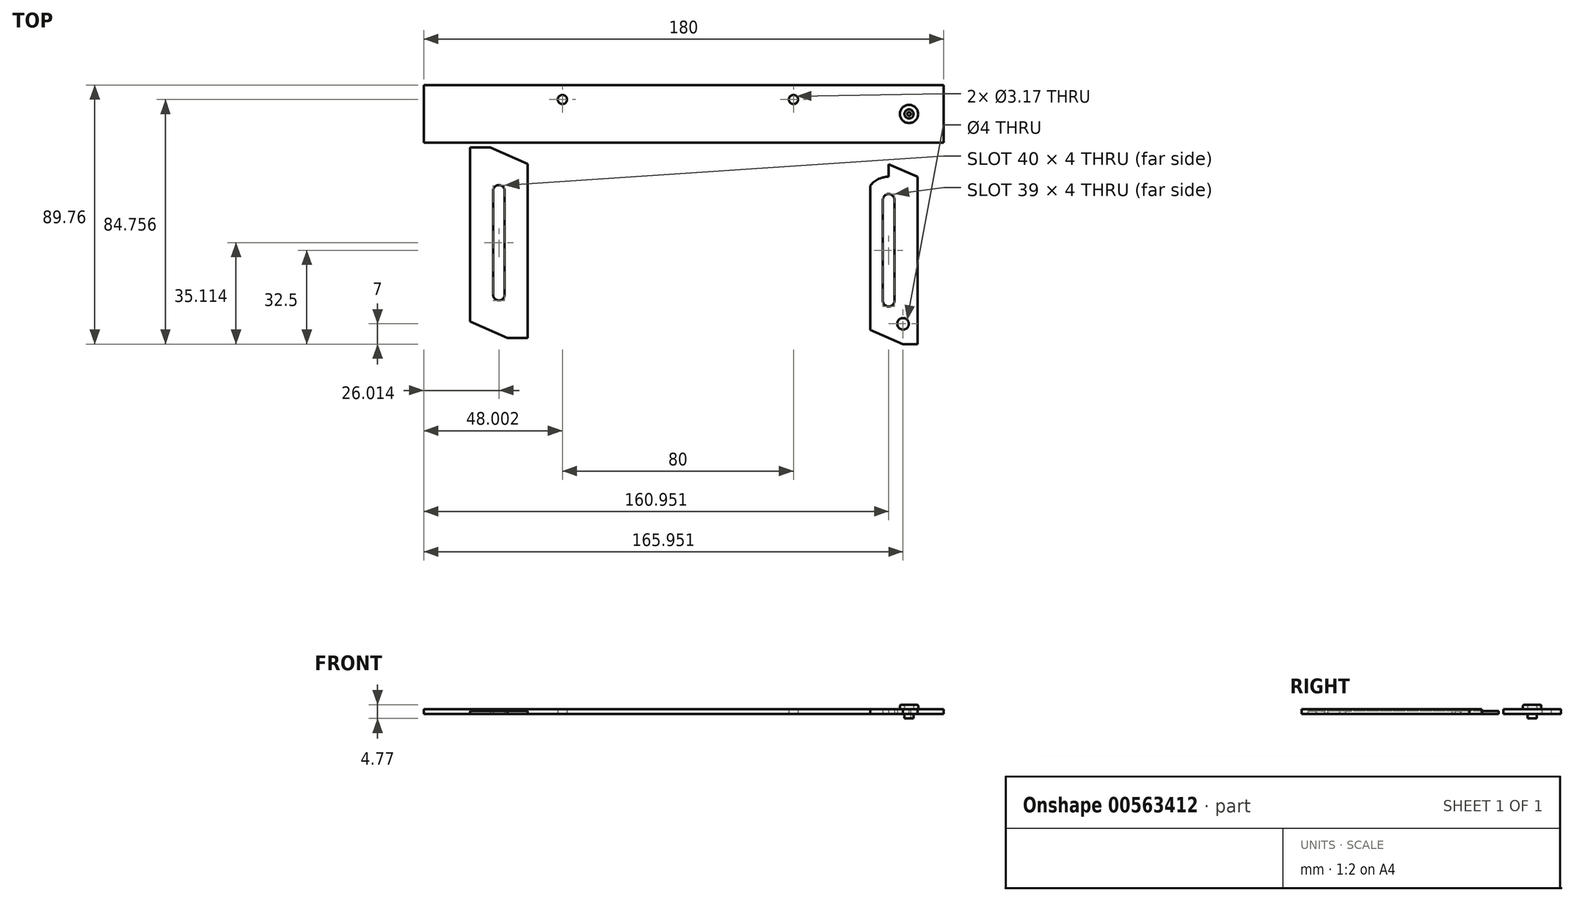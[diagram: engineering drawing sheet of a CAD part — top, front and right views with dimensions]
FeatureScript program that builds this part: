
annotation { "Feature Type Name" : "Feature", "Feature Type Description" : "" }
export const myFeature = defineFeature(function(context is Context, id is Id, definition is map)
    precondition{}
    {
        {
            var Q0;
            Q0=qCreatedBy(makeId("Top.planeOp"),FACE);
            var sketch = newSketch(context, id + "F0", { "sketchPlane" : qUnion([Q0])});
            skLineSegment(sketch, "E0.bottom", {"start": v(-55.85, 39.76) * mm, "end": v(124.15, 39.76) * mm});
            skLineSegment(sketch, "E0.top", {"start": v(-55.85, 19.76) * mm, "end": v(124.15, 19.76) * mm});
            skLineSegment(sketch, "E0.left", {"start": v(-55.85, 39.76) * mm, "end": v(-55.85, 19.76) * mm});
            skLineSegment(sketch, "E0.right", {"start": v(124.15, 39.76) * mm, "end": v(124.15, 19.76) * mm});
            skCircle(sketch, "E1", {"center": v(-7.85, 34.76) * mm, "radius": 1.59 * mm});
            skCircle(sketch, "E2", {"center": v(72.15, 34.76) * mm, "radius": 1.59 * mm});
            skCircle(sketch, "E3", {"center": v(112.15, 29.76) * mm, "radius": 1.59 * mm});
            skLineSegment(sketch, "E4", {"start": v(72.15, 34.76) * mm, "end": v(-7.85, 34.76) * mm, "construction": true});
            skSolve(sketch);
        }
        {
            var Q0;
            {var subQ1=sQuery(id+"F0.wireOp",EDGE,"E0.top");Q0=makeQuery(id+"F0.imprint","IMPRINT",FACE,{"disambiguationData":[TD([[makeQuery(id+"F0.imprint","IMPRINT",EDGE,{"derivedFrom":subQ1}),1.0]])]});}
            var Q1;
            {var subQ0=sQuery(id+"F0.wireOp",EDGE,"E0.left");Q1=makeQuery(id+"F0.imprint","IMPRINT",FACE,{"disambiguationData":[TD([[makeQuery(id+"F0.imprint","IMPRINT",EDGE,{"derivedFrom":subQ0}),1.0]])]});}
            var Q2;
            {var subQ0=sQuery(id+"F0.wireOp",EDGE,"wivM3JNJ-4vQW-bry1-dmZ1-3PybGXmywoTn");var subQ1=sQuery(id+"F0.wireOp",EDGE,"E0.top");var subQ2=makeQuery(id+"F0.imprint","INTERSECT",VERTEX,{"derivedFrom":[subQ1,subQ0]});Q2=makeQuery(id+"F0.imprint","IMPRINT",FACE,{"disambiguationData":[TD([[makeQuery(id+"F0.imprint","IMPRINT",EDGE,{"disambiguationData":[TD([[subQ2,1.0]])],"derivedFrom":subQ1}),-1.0]])]});}
            extrude(context, id + "F1", {"entities" : qUnion([Q0, Q1, Q2]), "depth" : 1.59 * mm, "offsetDistance" : 25.4 * mm});
        }
        {
            var Q0;
            Q0=qCreatedBy(makeId("Top.planeOp"),FACE);
            var sketch = newSketch(context, id + "F2", { "sketchPlane" : qUnion([Q0])});
            skLineSegment(sketch, "E5.bottom", {"start": v(98.75, 8) * mm, "end": v(115.1, 8) * mm});
            skLineSegment(sketch, "E5.left", {"start": v(98.75, 8) * mm, "end": v(98.75, -43) * mm});
            skCircle(sketch, "E6", {"center": v(105.1, 0) * mm, "radius": 2 * mm});
            skCircle(sketch, "E7", {"center": v(105.1, -35) * mm, "radius": 2 * mm});
            skLineSegment(sketch, "E8", {"start": v(107.1, 0) * mm, "end": v(107.1, -35) * mm});
            skLineSegment(sketch, "E9", {"start": v(103.1, 0) * mm, "end": v(103.1, -35) * mm});
            skLineSegment(sketch, "E10", {"start": v(115.1, 8) * mm, "end": v(115.1, -50) * mm});
            skLineSegment(sketch, "E11", {"start": v(98.75, -43) * mm, "end": v(115.1, -50) * mm});
            skLineSegment(sketch, "E12", {"start": v(105.1, 0) * mm, "end": v(105.1, 2) * mm});
            skLineSegment(sketch, "E13", {"start": v(105.1, 12.28) * mm, "end": v(98.75, 8) * mm});
            skCircle(sketch, "E14", {"center": v(110.1, -43) * mm, "radius": 2 * mm});
            skLineSegment(sketch, "E15.trimOffspring", {"start": v(105.1, 8) * mm, "end": v(105.1, 12.28) * mm});
            skLineSegment(sketch, "E16", {"start": v(105.1, 12.28) * mm, "end": v(115.1, 8) * mm});
            skCircle(sketch, "E17", {"center": v(105.1, 0) * mm, "radius": 8 * mm});
            skLineSegment(sketch, "E18", {"start": v(115.1, -50) * mm, "end": v(110.1, -50) * mm});
            skLineSegment(sketch, "E19", {"start": v(110.1, -50) * mm, "end": v(110.1, -47.86) * mm});
            skLineSegment(sketch, "E20", {"start": v(110.1, -50) * mm, "end": v(98.75, -45.14) * mm});
            skLineSegment(sketch, "E21", {"start": v(98.75, -45.14) * mm, "end": v(98.75, -43) * mm});
            skCircle(sketch, "E22", {"center": v(-29.84, -32.89) * mm, "radius": 2 * mm});
            skLineSegment(sketch, "E23", {"start": v(-19.84, -47.89) * mm, "end": v(-26.84, -47.89) * mm});
            skLineSegment(sketch, "E24", {"start": v(-26.84, -47.89) * mm, "end": v(-39.84, -42.2) * mm});
            skLineSegment(sketch, "E25", {"start": v(-29.84, -32.89) * mm, "end": v(-29.84, 18.38) * mm, "construction": true});
            skLineSegment(sketch, "E26", {"start": v(-21.84, -14.89) * mm, "end": v(-50.77, -14.89) * mm, "construction": true});
            skCircle(sketch, "E27", {"center": v(-29.84, 3.11) * mm, "radius": 2 * mm});
            skLineSegment(sketch, "E28", {"start": v(-39.84, 18.11) * mm, "end": v(-32.84, 18.11) * mm});
            skLineSegment(sketch, "E29", {"start": v(-32.84, 18.11) * mm, "end": v(-19.84, 12.43) * mm});
            skLineSegment(sketch, "E30", {"start": v(-39.84, 18.11) * mm, "end": v(-39.84, -42.2) * mm});
            skLineSegment(sketch, "E31", {"start": v(-19.84, 12.43) * mm, "end": v(-19.84, -47.89) * mm});
            skLineSegment(sketch, "E32", {"start": v(-27.84, 3.11) * mm, "end": v(-27.84, -32.89) * mm});
            skLineSegment(sketch, "E33", {"start": v(-31.83, 3.21) * mm, "end": v(-31.84, -32.89) * mm});
            skSolve(sketch);
        }
        {
            var Q0;
            {var subQ2=sQuery(id+"F2.wireOp",EDGE,"E15.trimOffspring");Q0=makeQuery(id+"F2.imprint","IMPRINT",FACE,{"disambiguationData":[TD([[makeQuery(id+"F2.imprint","IMPRINT",EDGE,{"derivedFrom":subQ2}),-1.0]])]});}
            var Q1;
            {var subQ11=sQuery(id+"F2.wireOp",EDGE,"E10");Q1=makeQuery(id+"F2.imprint","IMPRINT",FACE,{"disambiguationData":[TD([[makeQuery(id+"F2.imprint","IMPRINT",EDGE,{"derivedFrom":subQ11}),-1.0]])]});}
            var Q2;
            {var subQ1=sQuery(id+"F2.wireOp",EDGE,"E6");var subQ3=makeQuery(id+"F2.imprint","IMPRINT",VERTEX,{"derivedFrom":subQ1});Q2=makeQuery(id+"F2.imprint","IMPRINT",FACE,{"disambiguationData":[TD([[makeQuery(id+"F2.imprint","IMPRINT",EDGE,{"disambiguationData":[TD([[subQ3,1.0]])],"derivedFrom":subQ1}),-1.0]])]});}
            var Q3;
            {var subQ2=sQuery(id+"F2.wireOp",EDGE,"E19");Q3=makeQuery(id+"F2.imprint","IMPRINT",FACE,{"disambiguationData":[TD([[makeQuery(id+"F2.imprint","IMPRINT",EDGE,{"derivedFrom":subQ2}),1.0]])]});}
            var Q4;
            {var subQ0=sQuery(id+"F2.wireOp",EDGE,"E18");Q4=makeQuery(id+"F2.imprint","IMPRINT",FACE,{"disambiguationData":[TD([[makeQuery(id+"F2.imprint","IMPRINT",EDGE,{"derivedFrom":subQ0}),-1.0]])]});}
            extrude(context, id + "F3", {"entities" : qUnion([Q0, Q1, Q2, Q3, Q4]), "depth" : 1.59 * mm, "offsetDistance" : 25.4 * mm});
        }
        {
            var Q0;
            Q0=makeQuery(id+"F1.opExtrude","CAP_FACE",FACE,{"disambiguationData":[OSD([sQuery(id+"F0.wireOp",EDGE,"E0.bottom"),sQuery(id+"F0.wireOp",EDGE,"E0.top"),sQuery(id+"F0.wireOp",EDGE,"E0.left"),sQuery(id+"F0.wireOp",EDGE,"E0.right"),sQuery(id+"F0.wireOp",EDGE,"E1"),sQuery(id+"F0.wireOp",EDGE,"E2"),sQuery(id+"F0.wireOp",EDGE,"E3")])],"isStart":false});
            var sketch = newSketch(context, id + "F4", { "sketchPlane" : qUnion([Q0])});
            skCircle(sketch, "E34.0", {"center": v(112.15, 29.76) * mm, "radius": 1.59 * mm});
            skSolve(sketch);
        }
        {
            var Q0;
            Q0=makeQuery(id+"F4.imprint","IMPRINT",FACE,{"disambiguationData":[TD([[makeQuery(id+"F4.imprint","IMPRINT",EDGE,{"derivedFrom":sQuery(id+"F4.wireOp",EDGE,"E34.0")}),1.0]])]});
            extrude(context, id + "F5", {"entities" : qUnion([Q0]), "oppositeDirection" : true, "depth" : 3.17 * mm, "offsetDistance" : 25.4 * mm});
        }
        {
            var Q0;
            Q0=makeQuery(id+"F5.opExtrude","CAP_FACE",FACE,{"disambiguationData":[OSD([sQuery(id+"F4.wireOp",EDGE,"E34.0")])],"isStart":true});
            var sketch = newSketch(context, id + "F6", { "sketchPlane" : qUnion([Q0])});
            skCircle(sketch, "E35", {"center": v(112.15, 29.76) * mm, "radius": 3.18 * mm});
            skCircle(sketch, "E36", {"center": v(112.15, 29.76) * mm, "radius": 0.64 * mm});
            skSolve(sketch);
        }
        {
            var Q0;
            Q0=makeQuery(id+"F6.imprint","IMPRINT",FACE,{"disambiguationData":[TD([[makeQuery(id+"F6.imprint","IMPRINT",EDGE,{"derivedFrom":sQuery(id+"F6.wireOp",EDGE,"E35")}),1.0]])]});
            extrude(context, id + "F7", {"entities" : qUnion([Q0]), "operationType" : NewBodyOperationType.ADD, "depth" : 1.59 * mm, "offsetDistance" : 25.4 * mm});
        }
        {
            var Q0;
            Q0=makeQuery(id+"F6.imprint","IMPRINT",FACE,{"disambiguationData":[TD([[makeQuery(id+"F6.imprint","IMPRINT",EDGE,{"derivedFrom":sQuery(id+"F6.wireOp",EDGE,"E36")}),1.0]])]});
            extrude(context, id + "F8", {"entities" : qUnion([Q0]), "operationType" : NewBodyOperationType.REMOVE, "endBound" : BoundingType.THROUGH_ALL, "oppositeDirection" : true, "depth" : 25.4 * mm, "offsetDistance" : 25.4 * mm});
        }
        {
            var Q0;
            Q0=makeQuery(id+"F7.opExtrude","CAP_EDGE",EDGE,{"disambiguationData":[OSD([sQuery(id+"F4.wireOp",EDGE,"E34.0")])],"isStart":false});
            var Q1;
            Q1=makeQuery(id+"F7.opExtrude","CAP_EDGE",EDGE,{"disambiguationData":[OSD([sQuery(id+"F6.wireOp",EDGE,"E35")])],"isStart":false});
            fillet(context, id + "F9", {"entities" : qUnion([Q0, Q1]), "radius" : 0.5 * mm, "tangentPropagation" : true, "allowEdgeOverflow" : false});
        }
        {
            var Q0;
            Q0=makeQuery(id+"F2.imprint","IMPRINT",FACE,{"disambiguationData":[TD([[makeQuery(id+"F2.imprint","IMPRINT",EDGE,{"derivedFrom":sQuery(id+"F2.wireOp",EDGE,"E23")}),-1.0]])]});
            extrude(context, id + "F10", {"entities" : qUnion([Q0]), "depth" : 1 * mm, "offsetDistance" : 25 * mm});
        }
    });
